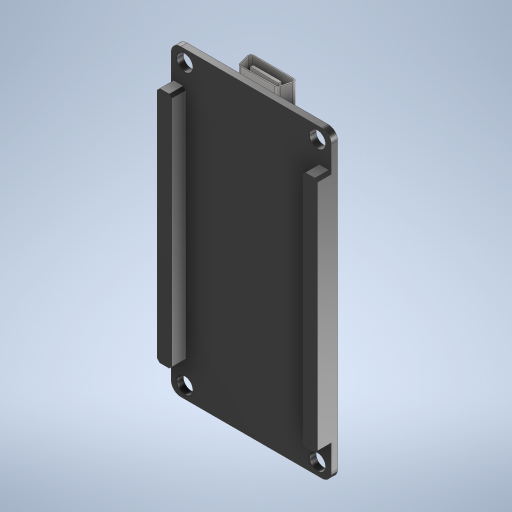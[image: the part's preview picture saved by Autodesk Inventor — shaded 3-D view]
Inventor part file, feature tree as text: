
AUTODESK INVENTOR PART (.ipt)
format: ipt  version: 2023 (Build 270158000, 158)  size: 486,912 bytes
history: native  units: mm
features: extrude x11, sketch x9, projected_geometry x3, fillet x2, other x1, mirror x1
ambient origin geometry x8: Origin, YZ Plane, XZ Plane, XY Plane, X Axis, Y Axis, Z Axis, Center Point
bodies: Body1 (feature_tree)
feature tree (27):
  other  "솔리드1"
  extrude  "돌출1"  Depth=25.33mm
  extrude  "돌출2"  Depth=48.0mm
  extrude  "돌출3"  Depth=2.5mm
  extrude  "돌출4"  Depth=1.9mm
  sketch  "스케치5"
  extrude  "돌출5"  Depth=21.0mm
  extrude  "돌출6"  Depth=1.0mm TaperAngle=0.0deg
  fillet  "모깎기1"  Radius=1.5mm
  extrude  "돌출7"  Depth=7.6mm
  extrude  "돌출8"  Depth=2.6mm
  mirror  "미러1"
  fillet  "모깎기2"  [1 undecoded]
  extrude  "돌출9"  Depth=0.5mm
  sketch  "스케치9"
  extrude  "돌출10"  Depth=0.5mm
  extrude  "돌출11"  Depth=0.2mm
  sketch  "스케치1"
  sketch  "스케치2"
  sketch  "스케치3"
  projected_geometry  "투영된 루프1"
  sketch  "스케치4"
  projected_geometry  "투영된 루프2"
  sketch  "스케치6"
  sketch  "스케치7"
  sketch  "스케치8"
  projected_geometry  "투영된 루프3"
note: 1 required parameter value undecoded (feature->parameter linkage not recoverable at this tier; creation-order binding heuristic only, values carry confidence <= 0.55)
